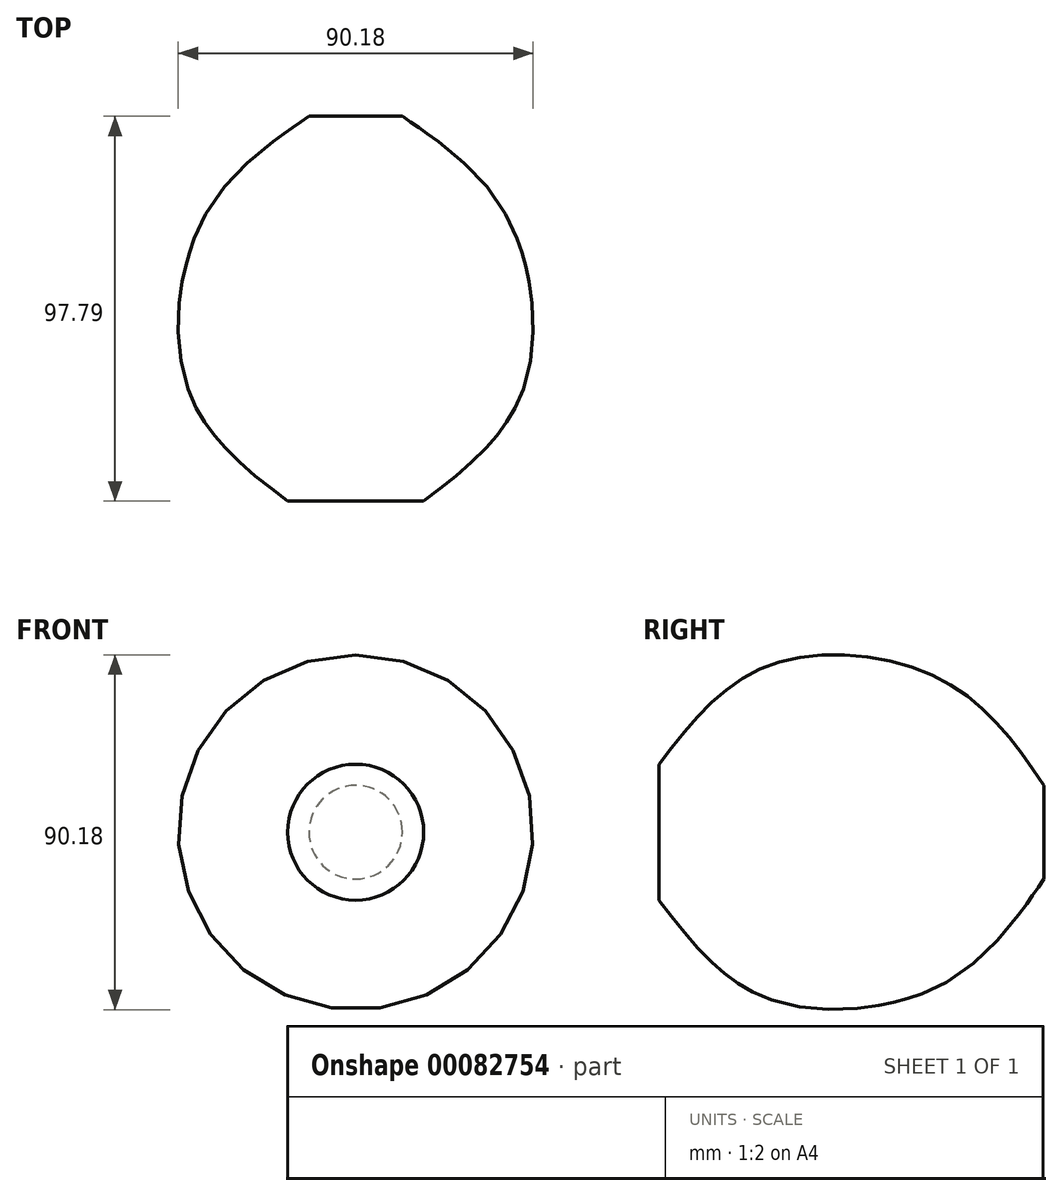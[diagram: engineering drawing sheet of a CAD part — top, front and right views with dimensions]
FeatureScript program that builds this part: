
annotation { "Feature Type Name" : "Feature", "Feature Type Description" : "" }
export const myFeature = defineFeature(function(context is Context, id is Id, definition is map)
    precondition{}
    {
        {
            var Q0;
            Q0=qCreatedBy(makeId("Top.planeOp"),FACE);
            var sketch = newSketch(context, id + "F0", { "sketchPlane" : qUnion([Q0])});
            skFitSpline(sketch, "E0", {"points": [v(11.88, 43.87) * mm, v(38.55, 18.22) * mm, v(42.34, -26.09) * mm, v(17.27, -53.92) * mm], "startDerivative": vector(95.3, -65.2) * mm, "endDerivative": vector(-95.06, -72.6) * mm});
            skLineSegment(sketch, "E1", {"start": v(11.88, 43.87) * mm, "end": v(0, 43.87) * mm});
            skLineSegment(sketch, "E2", {"start": v(0, 43.87) * mm, "end": v(0, -53.92) * mm});
            skLineSegment(sketch, "E3", {"start": v(0, -53.92) * mm, "end": v(17.27, -53.92) * mm});
            skSolve(sketch);
        }
        {
            var Q0;
            Q0=makeQuery(id+"F0.imprint","IMPRINT",FACE,{"disambiguationData":[TD([[makeQuery(id+"F0.imprint","IMPRINT",EDGE,{"derivedFrom":sQuery(id+"F0.wireOp",EDGE,"E0")}),-1.0]])]});
            var Q1;
            Q1=sQuery(id+"F0.wireOp",EDGE,"E2");
            revolve(context, id + "F1", {"entities" : qUnion([Q0]), "axis" : qUnion([Q1]), "revolveType" : RevolveType.FULL});
        }
    });
